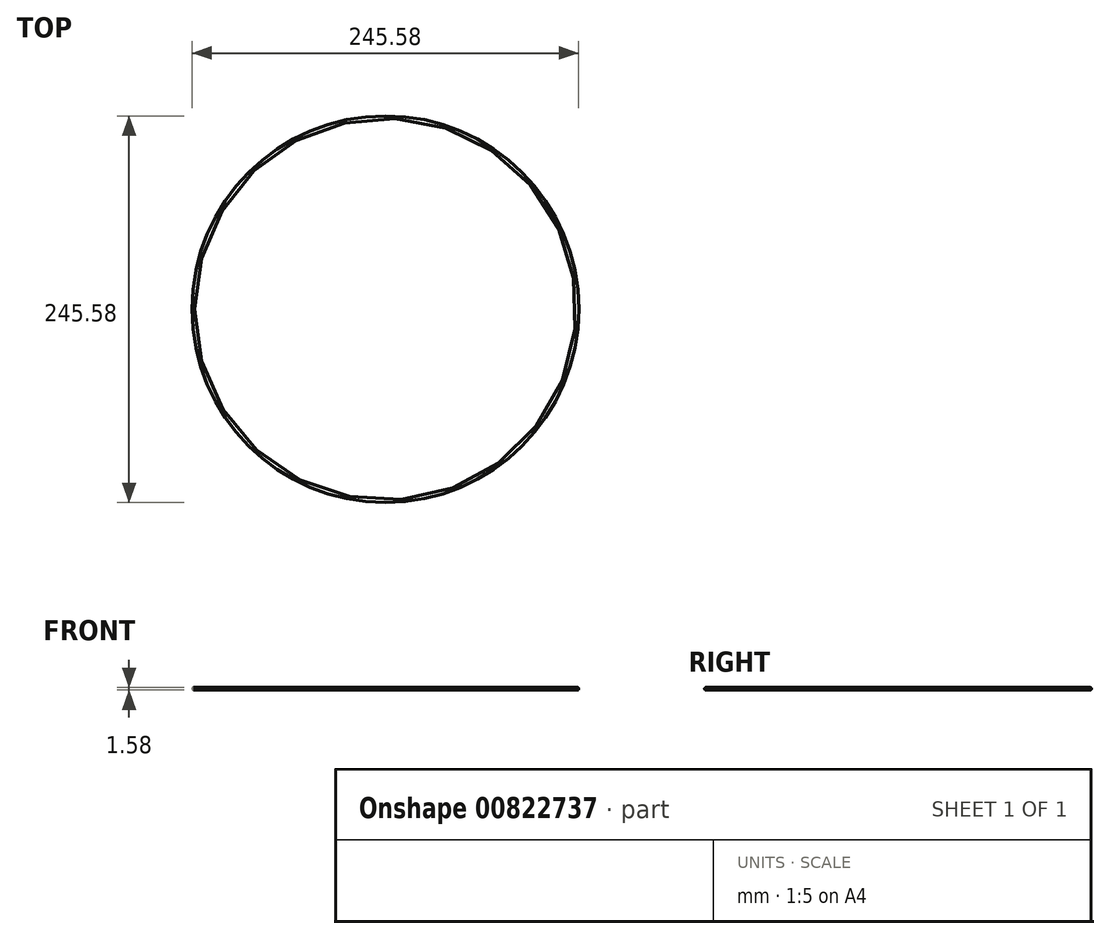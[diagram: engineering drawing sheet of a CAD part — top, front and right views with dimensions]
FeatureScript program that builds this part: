
annotation { "Feature Type Name" : "Feature", "Feature Type Description" : "" }
export const myFeature = defineFeature(function(context is Context, id is Id, definition is map)
    precondition{}
    {
        {
            var Q0;
            Q0=qCreatedBy(makeId("Front.planeOp"),FACE);
            var sketch = newSketch(context, id + "F0", { "sketchPlane" : qUnion([Q0])});
            skCircle(sketch, "E0", {"center": v(-122, 0) * mm, "radius": 0.8 * mm});
            skLineSegment(sketch, "E1", {"start": v(0, 0) * mm, "end": v(0, 61.07) * mm, "construction": true});
            skSolve(sketch);
        }
        {
            var Q0;
            Q0=makeQuery(id+"F0.imprint","IMPRINT",FACE,{"disambiguationData":[TD([[makeQuery(id+"F0.imprint","IMPRINT",EDGE,{"derivedFrom":sQuery(id+"F0.wireOp",EDGE,"E0")}),1.0]])]});
            var Q1;
            Q1=sQuery(id+"F0.wireOp",EDGE,"E1");
            revolve(context, id + "F1", {"surfaceOperationType" : NewSurfaceOperationType.NEW, "entities" : qUnion([Q0]), "axis" : qUnion([Q1]), "revolveType" : RevolveType.FULL});
        }
    });
